# Revit family: Free_Standing_Tub_Filler-American_Standard-Town_Square_S-T455951
name_source: partatom
category: Plumbing Fixtures
revit_build: Autodesk Revit 2014 (Build: 20130308_1515(x64)
units: mm (PartAtom-declared; Revit-internal decimal feet)

## types (1)
- T455951
    ADA Compliant = Yes
    Assembly Code = D2020300
    CW Connection = Yes
    CWFU = 3
    Cold Water Connection Diameter = 1/2"
    Default Elevation = 0"
    Description = T455951 Free Standing Tub Filler Personal Shower. Metal Lever Handle.
    Finish = Metal-American Standard-002-Polished Chrome
    Flow Rate = 1.8 gpm (6.8 L/min.)
    HW Connection = Yes
    HWFU = 3
    Height = 43 1/2"
    Hot Water Connection Diameter = 1"
    Installation Type = Surface Mounted
    Length = 7 5/32"
    Manufacturer = American Standard
    Material = Metal-American Standard-002-Polished Chrome
    Model = T455951
    Price = Prices may vary. Please consult Manufacturer Representative for most up-to-date price list.
    Product Documentation Link = https://www.americanstandard-us.com
    Product Page URL = https://www.americanstandard-us.com
    Specification = Free standing tub filler shall feature brass construction. Shall also feature 1/4 turn washerless ceramic disc valve cartridge.
    Tempered Water Connection Diameter = 1/2"
    URL = https://www.americanstandard-us.com
    Vent Connection = No
    WFU = 4
    Warranty Information = Limited Lifetime Warranty
    Waste Connection = No
    Width = 7"

## geometry (parser evidence)
native form markers: Sweep x3
no freeform markers — native parametric forms only
